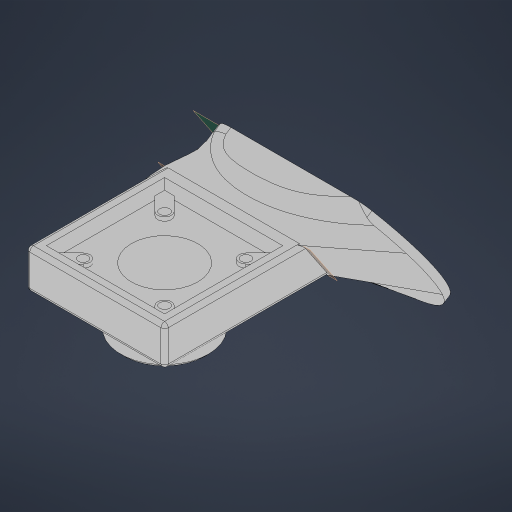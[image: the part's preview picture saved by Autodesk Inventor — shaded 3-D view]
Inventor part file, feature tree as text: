
AUTODESK INVENTOR PART (.ipt)
format: ipt  version: 2023 (Build 270158000, 158)  size: 487,936 bytes
history: native  units: in
note: dims shown in document units (in); Inventor stores cm internally (conversion verified against a paired STEP export)
features: sketch x10, extrude x7, hole x3, fillet x3, plane x2, projected_geometry x2, other x2, loft x1, chamfer x1
ambient origin geometry x8: Origin, YZ Plane, XZ Plane, XY Plane, X Axis, Y Axis, Z Axis, Center Point
bodies: Solid1 (feature_tree)
feature tree (31):
  extrude  "Extrusion1"  Depth=0.525in
  extrude  "Extrusion2"  Depth=0.3848in
  plane  "Work Plane1"
  extrude  "Extrusion3"  Depth=0.6in
  loft  "Loft1"
  extrude  "Extrusion4"  Depth=0.2in TaperAngle=0.0deg
  hole  "Hole1"  [1 undecoded]
  extrude  "Extrusion5"  Depth=0.1839in
  extrude  "Extrusion6"  Depth=0.05in TaperAngle=0.0deg
  hole  "Hole2"  [1 undecoded]
  plane  "Work Plane2"
  hole  "Hole3"  [1 undecoded]
  fillet  "Fillet1"  Radius=0.3in
  chamfer  "Chamfer1"  Distance=0.2in
  fillet  "Fillet2"  Radius=0.05in
  extrude  "Extrusion7"  Depth=0.05in TaperAngle=45.0deg
  fillet  "Fillet3"  Radius=0.0625in
  sketch  "Sketch1"  dims[d0=1.875in d1=0.525in]
  sketch  "Sketch2"  dims[d2=1.875in d3=0.0in d4=0.3848in]
  sketch  "Sketch3"  dims[d5=1.875in d6=0.0in d7=0.6in]
  sketch  "Sketch4"  dims[d10=0.1in d11=0.0in d14=0.0in d15=90.0deg]
  projected_geometry  "Projected Loop1"
  sketch  "Sketch5"  dims[d16=1.6in d17=0.2in d18=0.0in]
  sketch  "Sketch6"  dims[d19=0.9in d20=0.75in d21=0.119in d22=0.25in d23=0.6871in d24=1.0in d25=0.8108in d26=1.1875in]
  sketch  "Sketch7"  dims[d27=0.5in d28=0.0in d29=0.1839in]
  projected_geometry  "Projected Loop2"
  sketch  "Sketch8"  dims[d30=1.1024in d31=0.05in d32=0.0in]
  sketch  "Sketch9"  dims[d33=0.1339in d34=0.75in d35=0.185in d36=0.25in d37=0.6871in d38=1.0in d39=0.8108in d40=0.9792in]
  other  "Edges2"
  other  "Edges3"
  sketch  "Sketch10"  dims[d41=0.9792in d42=30.0deg d43=0.3in d44=0.2in d45=0.177in d46=0.75in d47=0.313in d48=0.45in d49=0.5635in d50=1.0in d51=0.8108in d52=0.05in d53=0.05in d54=0.125in d55=45.0deg d56=0.0625in d57=2.75in d58=0.0in d59=90.0deg d60=1.0in d61=0.5in d62=0.0in d63=0.25in]
note: 3 required parameter values undecoded (feature->parameter linkage not recoverable at this tier; creation-order binding heuristic only, values carry confidence <= 0.55)
